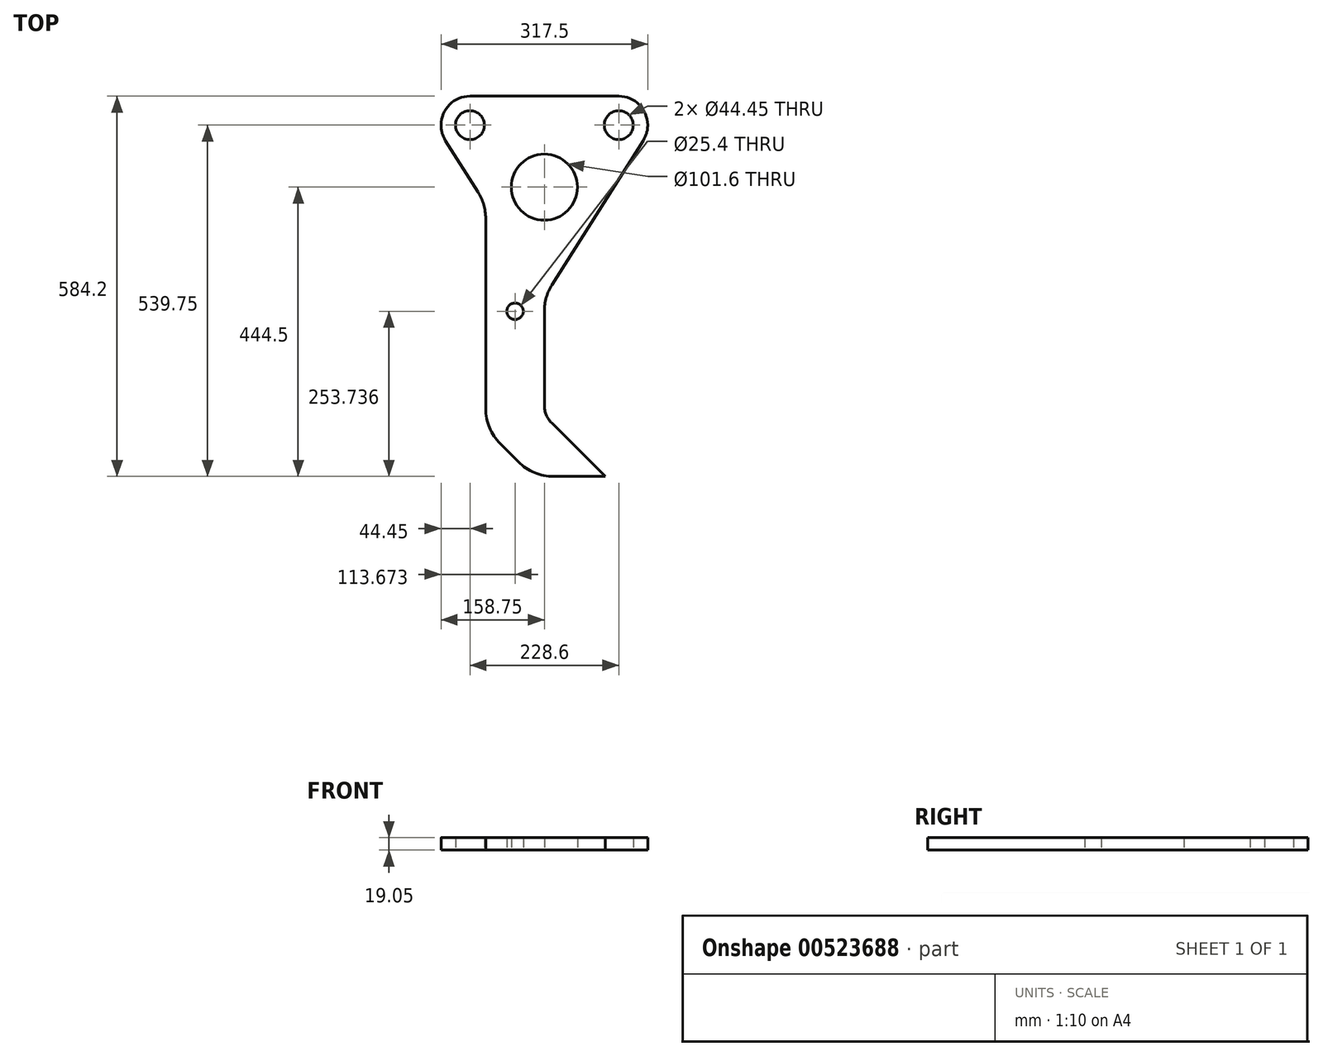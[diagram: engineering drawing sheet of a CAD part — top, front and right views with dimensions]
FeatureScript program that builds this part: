
annotation { "Feature Type Name" : "Feature", "Feature Type Description" : "" }
export const myFeature = defineFeature(function(context is Context, id is Id, definition is map)
    precondition{}
    {
        {
            var Q0;
            Q0=qCreatedBy(makeId("Top.planeOp"),FACE);
            var sketch = newSketch(context, id + "F0", { "sketchPlane" : qUnion([Q0])});
            skLineSegment(sketch, "E0.bottom", {"start": v(44.45, 0) * mm, "end": v(273.05, 0) * mm});
            skCircle(sketch, "E1", {"center": v(44.45, -44.45) * mm, "radius": 22.23 * mm});
            skCircle(sketch, "E2", {"center": v(273.05, -44.45) * mm, "radius": 22.23 * mm});
            skArc(sketch, "E3", {"start": v(0, -44.46) * mm, "mid": v(88.9, -44.45) * mm, "end": v(0, -44.44) * mm});
            skArc(sketch, "E4", {"start": v(317.5, -44.45) * mm, "mid": v(228.6, -44.45) * mm, "end": v(317.5, -44.45) * mm});
            skLineSegment(sketch, "E5", {"start": v(44.45, -88.9) * mm, "end": v(273.05, -88.9) * mm});
            skLineSegment(sketch, "E6", {"start": v(158.75, -330.46) * mm, "end": v(158.75, -474.8) * mm});
            skCircle(sketch, "E7", {"center": v(158.75, -139.7) * mm, "radius": 50.8 * mm});
            skCircle(sketch, "E8", {"center": v(158.75, -139.7) * mm, "radius": 90.15 * mm});
            skLineSegment(sketch, "E9", {"start": v(234.95, -187.88) * mm, "end": v(310.62, -68.2) * mm});
            skLineSegment(sketch, "E10", {"start": v(68.6, -187.88) * mm, "end": v(68.6, -479.91) * mm});
            skLineSegment(sketch, "E11", {"start": v(90.91, -533.8) * mm, "end": v(119, -561.88) * mm});
            skLineSegment(sketch, "E12", {"start": v(234.95, -187.88) * mm, "end": v(170.54, -289.74) * mm});
            skPoint(sketch, "E13.newPointA", {"position": v(158.75, -88.9) * mm});
            skLineSegment(sketch, "E14", {"start": v(170.11, -502.23) * mm, "end": v(252.08, -584.2) * mm});
            skLineSegment(sketch, "E15", {"start": v(252.08, -584.2) * mm, "end": v(172.88, -584.2) * mm});
            skPoint(sketch, "E16.visualSharp", {"position": v(68.6, -511.48) * mm});
            skArc(sketch, "E16.filletArc", {"start": v(68.6, -479.91) * mm, "mid": v(74.4, -509.07) * mm, "end": v(90.91, -533.8) * mm});
            skArc(sketch, "E17.filletArc", {"start": v(158.75, -474.8) * mm, "mid": v(161.7, -489.65) * mm, "end": v(170.11, -502.23) * mm});
            skPoint(sketch, "E18.visualSharp", {"position": v(141.32, -584.2) * mm});
            skArc(sketch, "E18.filletArc", {"start": v(119, -561.88) * mm, "mid": v(143.72, -578.4) * mm, "end": v(172.88, -584.2) * mm});
            skLineSegment(sketch, "E19", {"start": v(0, -44.44) * mm, "end": v(0, -44.46) * mm});
            skPoint(sketch, "E20.visualSharp", {"position": v(158.75, -308.4) * mm});
            skArc(sketch, "E20.filletArc", {"start": v(170.54, -289.74) * mm, "mid": v(161.76, -309.27) * mm, "end": v(158.75, -330.46) * mm});
            skLineSegment(sketch, "E21", {"start": v(317.5, -44.45) * mm, "end": v(317.5, -44.45) * mm});
            skLineSegment(sketch, "E22", {"start": v(6.88, -68.2) * mm, "end": v(56.8, -147.16) * mm});
            skArc(sketch, "E23.filletArc", {"start": v(68.6, -187.88) * mm, "mid": v(65.59, -166.68) * mm, "end": v(56.8, -147.16) * mm});
            skLineSegment(sketch, "E24", {"start": v(158.75, -330.46) * mm, "end": v(68.6, -330.46) * mm, "construction": true});
            skCircle(sketch, "E25", {"center": v(113.67, -330.46) * mm, "radius": 12.7 * mm});
            skSolve(sketch);
        }
        {
            var Q0;
            Q0 = qSketchRegion(id + "F0", true);
            var Q1;
            {var subQ0=sQuery(id+"F0.wireOp",EDGE,"E5");var subQ1=makeQuery(id+"F0.imprint","INTERSECT",VERTEX,{"derivedFrom":[subQ0,sQuery(id+"F0.wireOp",EDGE,"E7")]});Q1=makeQuery(id+"F0.imprint","IMPRINT",FACE,{"disambiguationData":[TD([[makeQuery(id+"F0.imprint","IMPRINT",EDGE,{"disambiguationData":[TD([[subQ1,-1.0]])],"derivedFrom":subQ0}),1.0]])]});}
            extrude(context, id + "F1", {"entities" : qUnion([Q0, Q1]), "depth" : 19.05 * mm, "offsetDistance" : 25.4 * mm});
        }
    });
